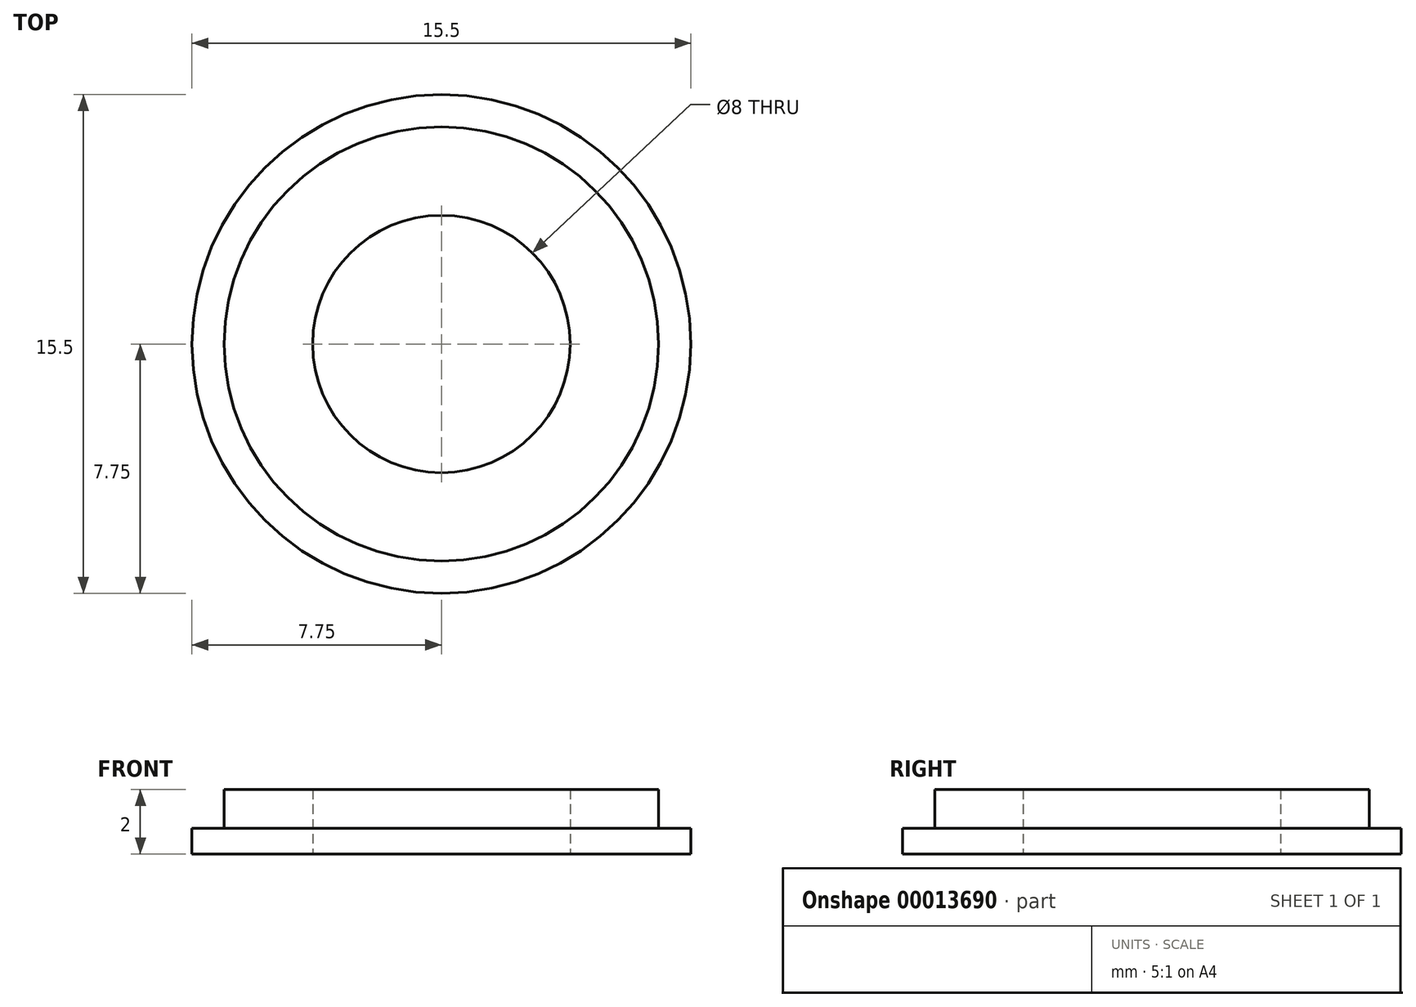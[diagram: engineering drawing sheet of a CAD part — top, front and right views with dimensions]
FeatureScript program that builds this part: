
annotation { "Feature Type Name" : "Feature", "Feature Type Description" : "" }
export const myFeature = defineFeature(function(context is Context, id is Id, definition is map)
    precondition{}
    {
        {
            var Q0;
            Q0=qCreatedBy(makeId("Top.planeOp"),FACE);
            var sketch = newSketch(context, id + "F0", { "sketchPlane" : qUnion([Q0])});
            skCircle(sketch, "E0", {"center": v(0, 0) * mm, "radius": 6.75 * mm});
            skCircle(sketch, "E1", {"center": v(0, 0) * mm, "radius": 4 * mm});
            skCircle(sketch, "E2", {"center": v(0, 0) * mm, "radius": 7.75 * mm});
            skSolve(sketch);
        }
        {
            var Q0;
            Q0=makeQuery(id+"F0.imprint","IMPRINT",FACE,{"disambiguationData":[TD([[makeQuery(id+"F0.imprint","IMPRINT",EDGE,{"derivedFrom":sQuery(id+"F0.wireOp",EDGE,"E0")}),1.0]])]});
            extrude(context, id + "F1", {"entities" : qUnion([Q0]), "depth" : 1.2 * mm});
        }
        {
            var Q0;
            Q0=makeQuery(id+"F0.imprint","IMPRINT",FACE,{"disambiguationData":[TD([[makeQuery(id+"F0.imprint","IMPRINT",EDGE,{"derivedFrom":sQuery(id+"F0.wireOp",EDGE,"E0")}),-1.0]])]});
            var Q1;
            Q1=makeQuery(id+"F0.imprint","IMPRINT",FACE,{"disambiguationData":[TD([[makeQuery(id+"F0.imprint","IMPRINT",EDGE,{"derivedFrom":sQuery(id+"F0.wireOp",EDGE,"E0")}),1.0]])]});
            extrude(context, id + "F2", {"entities" : qUnion([Q0, Q1]), "operationType" : NewBodyOperationType.ADD, "oppositeDirection" : true, "depth" : 0.8 * mm});
        }
    });
